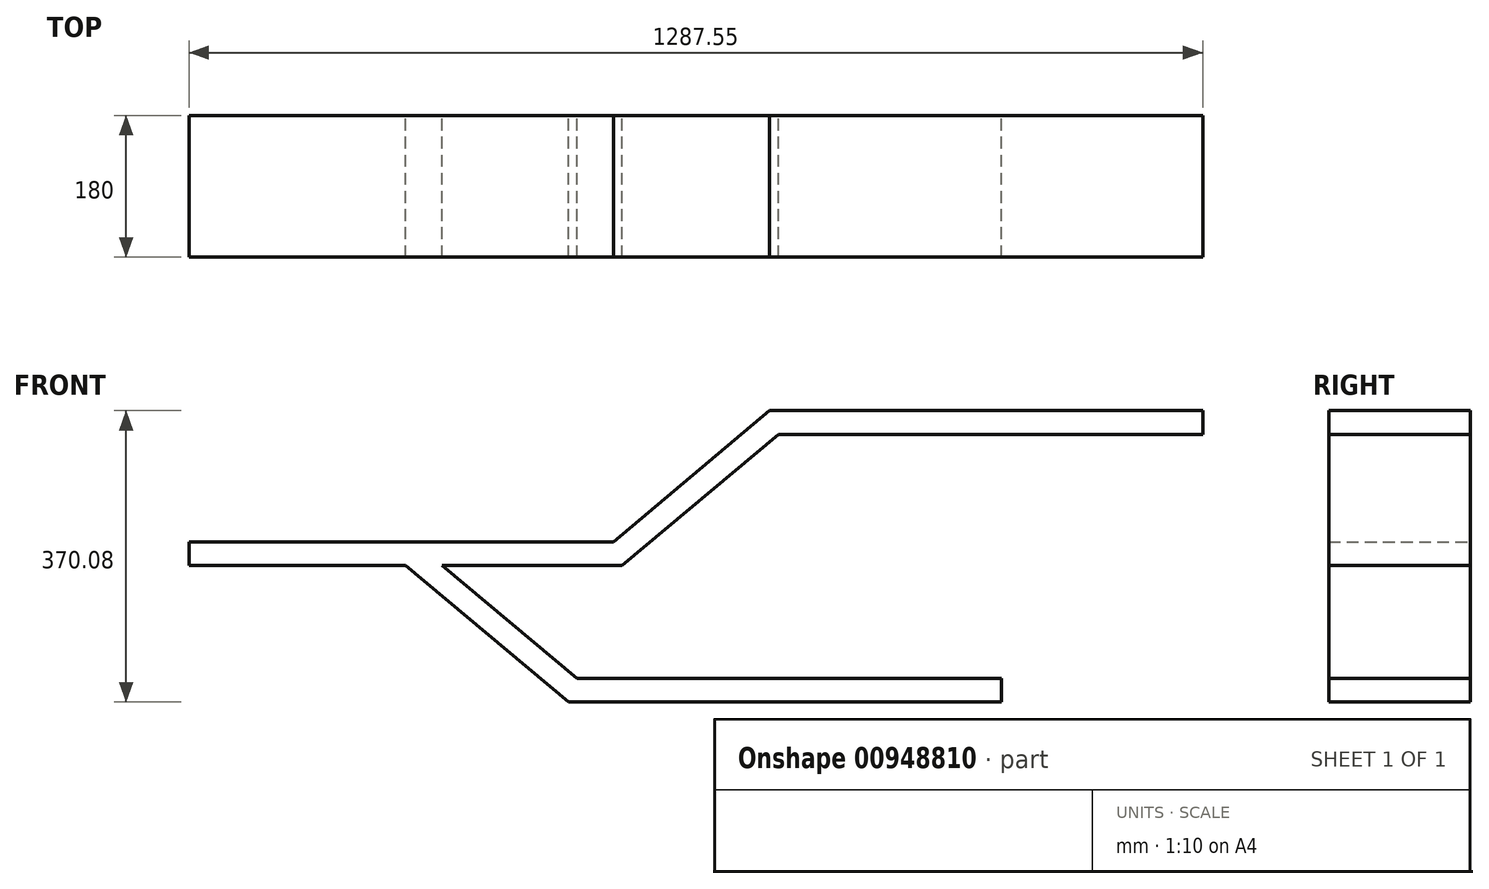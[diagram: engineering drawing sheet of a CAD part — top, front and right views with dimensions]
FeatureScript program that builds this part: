
annotation { "Feature Type Name" : "Feature", "Feature Type Description" : "" }
export const myFeature = defineFeature(function(context is Context, id is Id, definition is map)
    precondition{}
    {
        {
            var Q0;
            Q0=qCreatedBy(makeId("Front.planeOp"),FACE);
            var sketch = newSketch(context, id + "F0", { "sketchPlane" : qUnion([Q0])});
            skLineSegment(sketch, "E0", {"start": v(0, -30) * mm, "end": v(0, 0) * mm});
            skLineSegment(sketch, "E1", {"start": v(0, 0) * mm, "end": v(539.08, 0) * mm});
            skLineSegment(sketch, "E2", {"start": v(539.08, 0) * mm, "end": v(737.55, 166.53) * mm});
            skLineSegment(sketch, "E3", {"start": v(737.55, 166.53) * mm, "end": v(1287.55, 166.53) * mm});
            skLineSegment(sketch, "E4", {"start": v(1287.55, 166.53) * mm, "end": v(1287.55, 136.53) * mm});
            skLineSegment(sketch, "E5", {"start": v(1287.55, 136.53) * mm, "end": v(748.47, 136.53) * mm});
            skLineSegment(sketch, "E6", {"start": v(748.47, 136.53) * mm, "end": v(550, -30) * mm});
            skLineSegment(sketch, "E7", {"start": v(550, -30) * mm, "end": v(0, -30) * mm});
            skLineSegment(sketch, "E8", {"start": v(748.47, 136.53) * mm, "end": v(737.55, 166.53) * mm});
            skLineSegment(sketch, "E9", {"start": v(550, -30) * mm, "end": v(539.08, 0) * mm});
            skLineSegment(sketch, "E10", {"start": v(275, -30) * mm, "end": v(481.83, -203.55) * mm});
            skLineSegment(sketch, "E11", {"start": v(481.83, -203.55) * mm, "end": v(1031.83, -203.55) * mm});
            skLineSegment(sketch, "E12", {"start": v(1031.83, -203.55) * mm, "end": v(1031.83, -173.55) * mm});
            skLineSegment(sketch, "E13", {"start": v(1031.83, -173.55) * mm, "end": v(492.75, -173.55) * mm});
            skLineSegment(sketch, "E14", {"start": v(492.75, -173.55) * mm, "end": v(321.67, -30) * mm});
            skLineSegment(sketch, "E15", {"start": v(481.83, -203.55) * mm, "end": v(492.75, -173.55) * mm});
            skLineSegment(sketch, "E16", {"start": v(550, -30) * mm, "end": v(451.72, 87.13) * mm, "construction": true});
            skLineSegment(sketch, "E17", {"start": v(737.55, 166.53) * mm, "end": v(797.71, 94.83) * mm, "construction": true});
            skSolve(sketch);
        }
        {
            var Q0;
            Q0 = qSketchRegion(id + "F0", true);
            extrude(context, id + "F1", {"entities" : qUnion([Q0]), "depth" : 180 * mm, "offsetDistance" : 25 * mm});
        }
    });
